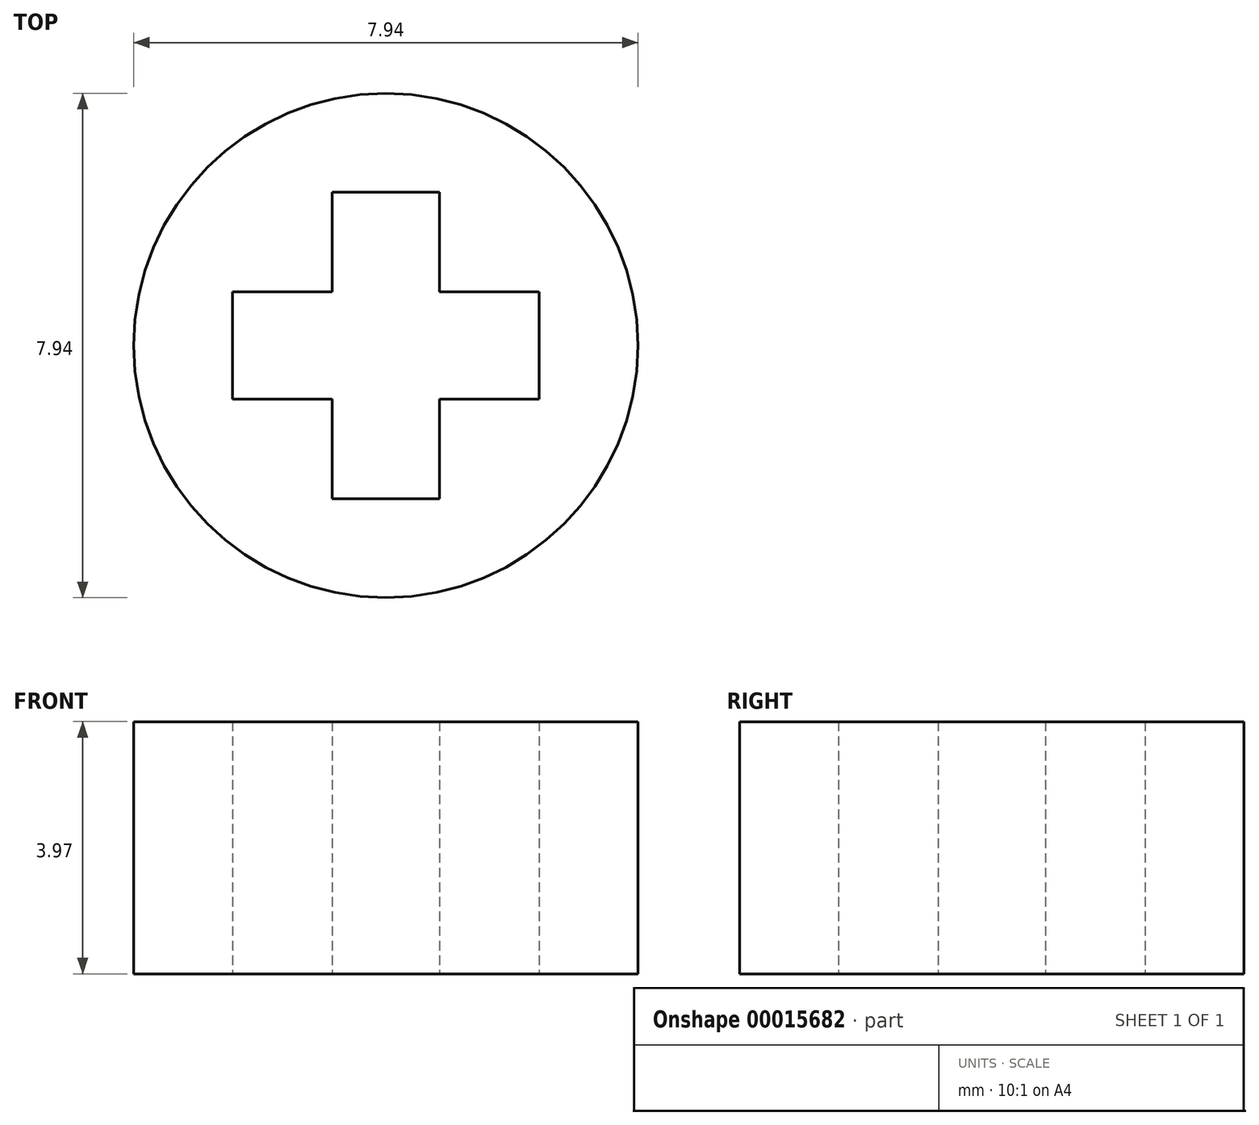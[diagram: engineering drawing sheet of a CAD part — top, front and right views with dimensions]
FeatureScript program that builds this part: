
annotation { "Feature Type Name" : "Feature", "Feature Type Description" : "" }
export const myFeature = defineFeature(function(context is Context, id is Id, definition is map)
    precondition{}
    {
        {
            var Q0;
            Q0=qCreatedBy(makeId("Top.planeOp"),FACE);
            var sketch = newSketch(context, id + "F0", { "sketchPlane" : qUnion([Q0])});
            skCircle(sketch, "E0", {"center": v(0, 0) * mm, "radius": 3.97 * mm});
            skLineSegment(sketch, "E1.rect.bottom", {"start": v(0.84, -2.41) * mm, "end": v(-0.84, -2.41) * mm});
            skLineSegment(sketch, "E1.rect.top", {"start": v(0.84, 2.41) * mm, "end": v(-0.84, 2.41) * mm});
            skLineSegment(sketch, "E1.rect.left", {"start": v(0.84, -2.41) * mm, "end": v(0.84, 2.41) * mm});
            skLineSegment(sketch, "E1.rect.right", {"start": v(-0.84, -2.41) * mm, "end": v(-0.84, 2.41) * mm});
            skLineSegment(sketch, "E2.rect.bottom", {"start": v(2.41, 0.84) * mm, "end": v(-2.41, 0.84) * mm});
            skLineSegment(sketch, "E2.rect.top", {"start": v(2.41, -0.84) * mm, "end": v(-2.41, -0.84) * mm});
            skLineSegment(sketch, "E2.rect.left", {"start": v(2.41, 0.84) * mm, "end": v(2.41, -0.84) * mm});
            skLineSegment(sketch, "E2.rect.right", {"start": v(-2.41, 0.84) * mm, "end": v(-2.41, -0.84) * mm});
            skSolve(sketch);
        }
        {
            var Q0;
            Q0 = qSketchRegion(id + "F0", true);
            extrude(context, id + "F1", {"entities" : qUnion([Q0]), "depth" : 3.97 * mm});
        }
    });
